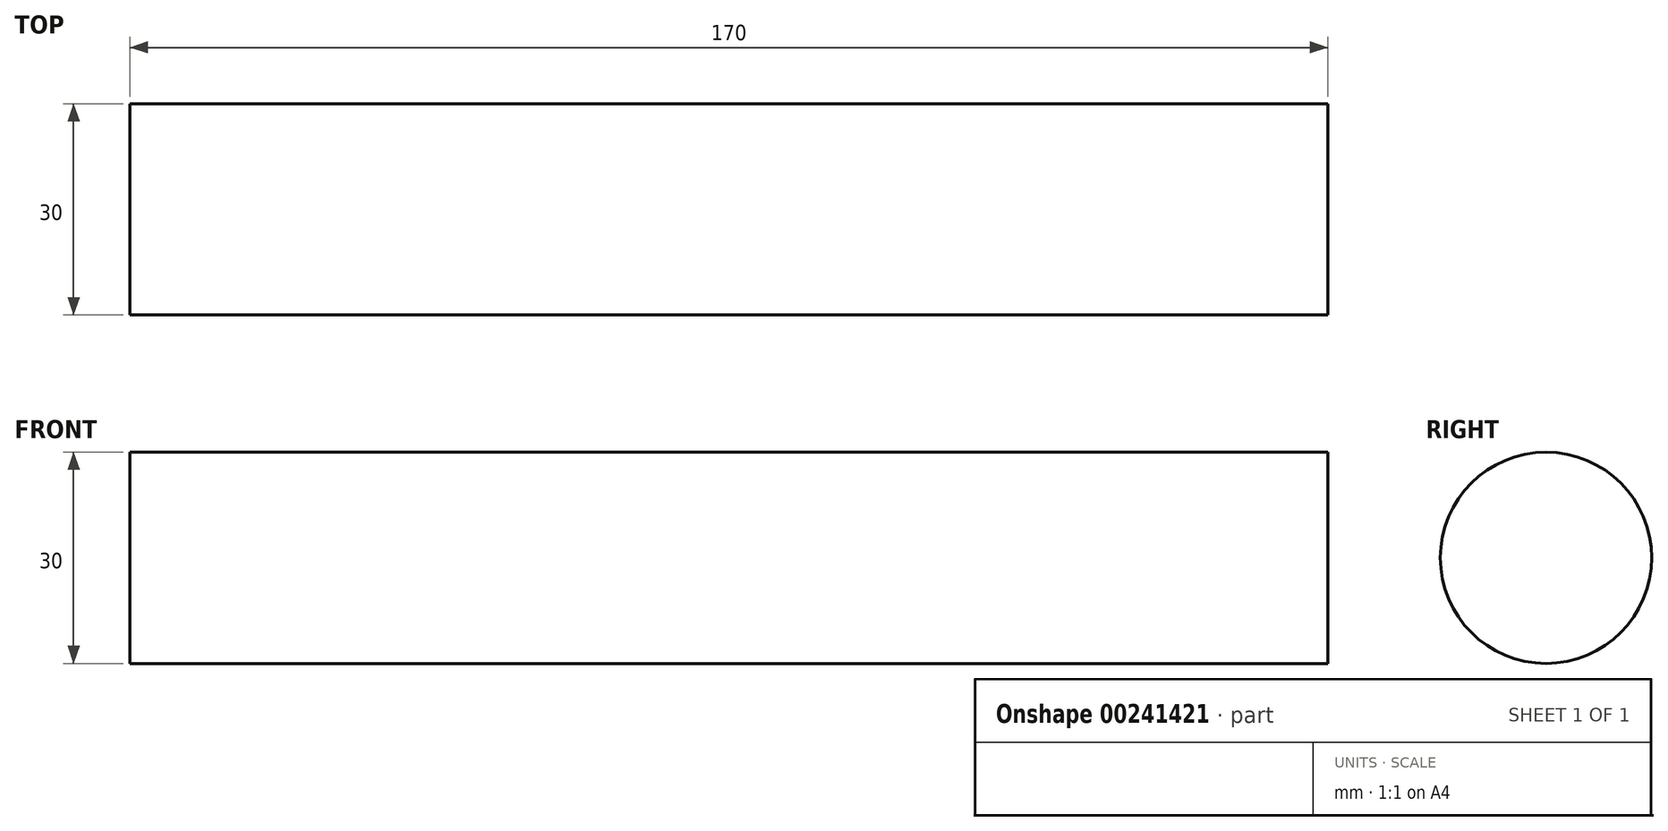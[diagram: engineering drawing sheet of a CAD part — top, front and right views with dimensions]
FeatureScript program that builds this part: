
annotation { "Feature Type Name" : "Feature", "Feature Type Description" : "" }
export const myFeature = defineFeature(function(context is Context, id is Id, definition is map)
    precondition{}
    {
        {
            var Q0;
            Q0=qCreatedBy(makeId("Right.planeOp"),FACE);
            var sketch = newSketch(context, id + "F0", { "sketchPlane" : qUnion([Q0])});
            skCircle(sketch, "E0", {"center": v(0, 0) * mm, "radius": 15 * mm});
            skSolve(sketch);
        }
        {
            var Q0;
            Q0 = qSketchRegion(id + "F0", true);
            extrude(context, id + "F1", {"entities" : qUnion([Q0]), "depth" : 170 * mm});
        }
    });
